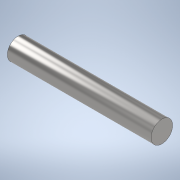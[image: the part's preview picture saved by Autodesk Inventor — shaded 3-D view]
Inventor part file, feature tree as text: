
AUTODESK INVENTOR PART (.ipt)
format: ipt  version: 2022 (Build 260153000, 153)  size: 99,840 bytes
history: native  units: mm
features: extrude x1, sketch x1
ambient origin geometry x8: Origin, YZ Plane, XZ Plane, XY Plane, X Axis, Y Axis, Z Axis, Center Point
bodies: 实体1 (feature_tree)
feature tree (2):
  extrude  "拉伸1"  Depth=20.0mm TaperAngle=0.0deg
  sketch  "草图1"  dims[d0=3.0mm d1=20.0mm d2=0.0mm]
